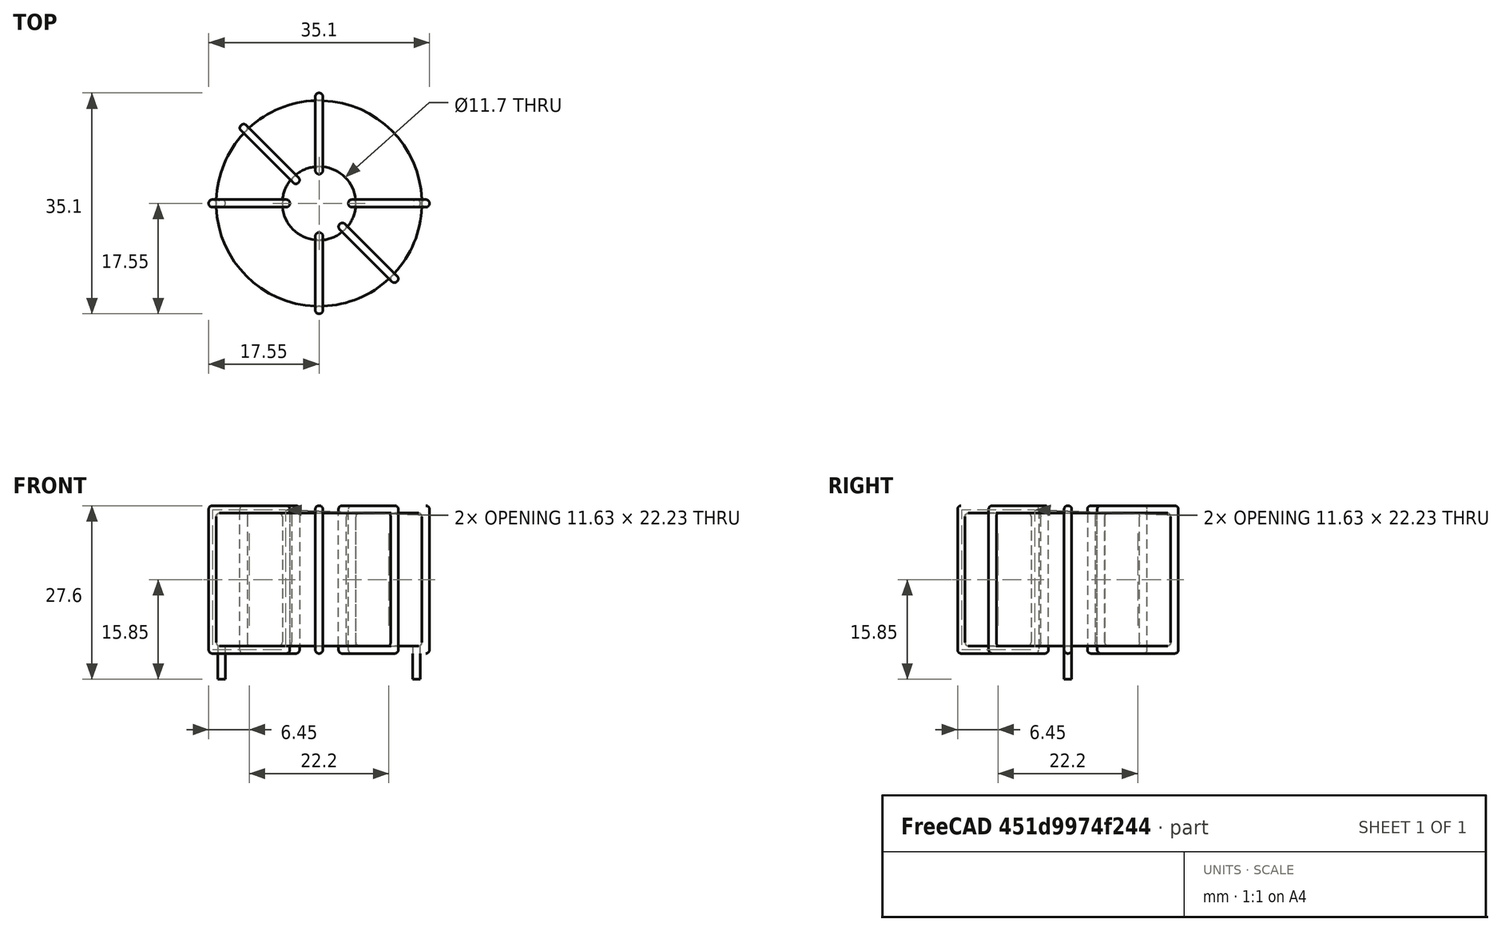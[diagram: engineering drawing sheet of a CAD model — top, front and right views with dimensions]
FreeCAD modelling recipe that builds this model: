
FCSTD DOCUMENT  (FreeCAD 0.16R6703 (Git))
Label: L_Toroid_Horizontal_D35.1mm_P31.00mm_Vishay_TJ6
License: All rights reserved
LicenseURL: http://en.wikipedia.org/wiki/All_rights_reserved
objects: Sketcher::SketchObject×6, PartDesign::Pad×6, PartDesign::Fillet×5, Spreadsheet::Sheet×1
note: 23 computed .brp shape members not serialized (recipe doc carries the construction recipe); baked Part::Feature solids carry a one-line shape summary decoded from their .brp

FEATURE [Spreadsheet::Sheet] Spreadsheet  label="dimensions"
  cells = A1=Wx; B1(Wx)=35.1; C1(WW)=11.7; D1=35.1; A2=Wy; B2(Wy)=35.1; D2=35.1; A3=RM; B3(RMx)=31; C3(RMy)=0; A4=d_wire; B4(d_wire)=1.2; A5=H; B5(H)=21.1; A6=offsetx; B6(offsetx)=2.050000000000001
FEATURE [Sketcher::SketchObject] Sketch
  Placement = pos=(0,0,1.7) rot=(0,0,1;0rad)
  expr: Placement.Base.z = 0.5 + Spreadsheet.d_wire
  expr: Constraints[0] = Spreadsheet.Wx / 2 - Spreadsheet.d_wire
  expr: Constraints[4] = Spreadsheet.WW / 2
  expr: Constraints[2] = Spreadsheet.RMy / 2
  expr: Constraints[1] = Spreadsheet.RMx / 2
  sketch-geometry (2):
    g0: Circle CenterX=15.5 CenterY=0 CenterZ=0 NormalX=0 NormalY=0 NormalZ=1 Radius=16.35
    g1: Circle CenterX=15.5 CenterY=0 CenterZ=0 NormalX=0 NormalY=0 NormalZ=1 Radius=5.85
  constraints (5):
    c: Radius(g0) = 16.35
    c: DistanceX(g-1,g0) = 15.5
    c: DistanceY(g-1,g0) = 0
    c: Coincident(g1,g0)
    c: Radius(g1) = 5.85
FEATURE [PartDesign::Pad] Pad
  Length = 21.1
  Length2 = 100
  Placement = pos=(0,0,1.7) rot=(0,0,1;0rad)
  Sketch = -> Sketch
  Type = 0
  expr: Length = Spreadsheet.H
FEATURE [Sketcher::SketchObject] Sketch001
  Placement = pos=(0,0,1.1) rot=(0,0,1;0rad)
  expr: Placement.Base.z = 0.5 + Spreadsheet.d_wire * 0.5
  expr: Constraints[4] = Spreadsheet.RMx
  expr: Constraints[2] = Spreadsheet.RMy
  expr: Constraints[1] = Spreadsheet.d_wire / 2
  sketch-geometry (2):
    g0: Circle CenterX=0 CenterY=0 CenterZ=0 NormalX=0 NormalY=0 NormalZ=1 Radius=0.6
    g1: Circle CenterX=31 CenterY=0 CenterZ=0 NormalX=0 NormalY=0 NormalZ=1 Radius=0.6
  constraints (5):
    c: Equal(g0,g1)
    c: Radius(g0) = 0.6
    c: DistanceY(g-1,g1) = 0
    c: Coincident(g0,g-1)
    c: DistanceX(g-1,g1) = 31
FEATURE [PartDesign::Pad] Pad001
  Length = 0.6
  Length2 = 4.7
  Placement = pos=(0,0,1.1) rot=(0,0,1;0rad)
  Reversed = true
  Sketch = -> Sketch001
  Type = 4
  expr: Length2 = 3.5 + Spreadsheet.d_wire
  expr: Length = Spreadsheet.d_wire / 2
FEATURE [PartDesign::Fillet] Fillet
  Base = -> Pad [Edge6,Edge3,Edge2]
  Placement = pos=(0,0,1.7) rot=(0,0,1;0rad)
  Radius = 0.5
FEATURE [Sketcher::SketchObject] Sketch003
  Placement = pos=(15.5,0,0) rot=(1,0,0;1.5708rad)
  expr: Placement.Base.x = Spreadsheet.RMx / 2
  expr: Constraints[49] = Spreadsheet.Wx - Spreadsheet.d_wire * 2
  expr: Constraints[44] = Spreadsheet.d_wire
  expr: Constraints[23] = Spreadsheet.H
  expr: Constraints[22] = Spreadsheet.Wx / 2 - Spreadsheet.d_wire
  expr: Placement.Base.y = Spreadsheet.RMy / 2
  expr: Constraints[21] = (Spreadsheet.Wx - Spreadsheet.WW) / 2 - Spreadsheet.d_wire
  expr: Constraints[19] = Spreadsheet.d_wire
  expr: Constraints[17] = Spreadsheet.d_wire
  expr: Constraints[18] = Spreadsheet.d_wire
  expr: Constraints[16] = Spreadsheet.d_wire
  sketch-geometry (16):
    g0: LineSegment StartX=-4.65 StartY=0.5 StartZ=0 EndX=-17.55 EndY=0.5 EndZ=0
    g1: LineSegment StartX=-17.55 StartY=0.5 StartZ=0 EndX=-17.55 EndY=24 EndZ=0
    g2: LineSegment StartX=-17.55 StartY=24 StartZ=0 EndX=-4.65 EndY=24 EndZ=0
    g3: LineSegment StartX=-4.65 StartY=24 StartZ=0 EndX=-4.65 EndY=0.5 EndZ=0
    g4: LineSegment StartX=-16.35 StartY=22.8 StartZ=0 EndX=-5.85 EndY=22.8 EndZ=0
    g5: LineSegment StartX=-5.85 StartY=22.8 StartZ=0 EndX=-5.85 EndY=1.7 EndZ=0
    g6: LineSegment StartX=-5.85 StartY=1.7 StartZ=0 EndX=-16.35 EndY=1.7 EndZ=0
    g7: LineSegment StartX=-16.35 StartY=1.7 StartZ=0 EndX=-16.35 EndY=22.8 EndZ=0
    g8: LineSegment StartX=4.65 StartY=24 StartZ=0 EndX=17.55 EndY=24 EndZ=0
    g9: LineSegment StartX=17.55 StartY=24 StartZ=0 EndX=17.55 EndY=0.5 EndZ=0
    g10: LineSegment StartX=17.55 StartY=0.5 StartZ=0 EndX=4.65 EndY=0.5 EndZ=0
    g11: LineSegment StartX=4.65 StartY=0.5 StartZ=0 EndX=4.65 EndY=24 EndZ=0
    g12: LineSegment StartX=5.85 StartY=22.8 StartZ=0 EndX=16.35 EndY=22.8 EndZ=0
    g13: LineSegment StartX=16.35 StartY=22.8 StartZ=0 EndX=16.35 EndY=1.7 EndZ=0
    g14: LineSegment StartX=16.35 StartY=1.7 StartZ=0 EndX=5.85 EndY=1.7 EndZ=0
    g15: LineSegment StartX=5.85 StartY=1.7 StartZ=0 EndX=5.85 EndY=22.8 EndZ=0
  constraints (50):
    c: Horizontal(g0)
    c: Coincident(g1,g0)
    c: Vertical(g1)
    c: Coincident(g2,g1)
    c: Horizontal(g2)
    c: Coincident(g3,g2)
    c: Coincident(g3,g0)
    c: Vertical(g3)
    c: Coincident(g4,g5)
    c: Coincident(g5,g6)
    c: Coincident(g6,g7)
    c: Coincident(g7,g4)
    c: Horizontal(g4)
    c: Horizontal(g6)
    c: Vertical(g5)
    c: Vertical(g7)
    c: DistanceX(g1,g4) = 1.2
    c: DistanceY(g4,g1) = 1.2
    c: DistanceX(g5,g0) = 1.2
    c: DistanceY(g0,g5) = 1.2
    c: DistanceY(g-1,g0) = 0.5
    c: DistanceX(g6,g6) = 10.5
    c: DistanceX(g6,g-1) = 16.35
    c: DistanceY(g7,g7) = 21.1
    c: Coincident(g8,g9)
    c: Coincident(g9,g10)
    c: Coincident(g10,g11)
    c: Coincident(g11,g8)
    c: Horizontal(g8)
    c: Horizontal(g10)
    c: Vertical(g9)
    c: Vertical(g11)
    c: Coincident(g12,g13)
    c: Coincident(g13,g14)
    c: Coincident(g14,g15)
    c: Coincident(g15,g12)
    c: Horizontal(g12)
    c: Horizontal(g14)
    c: Vertical(g13)
    c: Vertical(g15)
    c: DistanceY(g8,g2) = 0
    c: DistanceY(g10,g0) = 0
    c: DistanceY(g14,g5) = 0
    c: DistanceY(g12,g4) = 0
    c: DistanceX(g8,g12) = 1.2
    c: Equal(g8,g2)
    c: Equal(g12,g4)
    c: Equal(g9,g1)
    c: Equal(g13,g7)
    c: DistanceX(g4,g12) = 32.7
FEATURE [PartDesign::Pad] Pad002
  Length = 1.2
  Length2 = 100
  Midplane = true
  Placement = pos=(15.5,0,0) rot=(1,0,0;1.5708rad)
  Sketch = -> Sketch003
  Type = 0
  expr: Length = Spreadsheet.d_wire
FEATURE [PartDesign::Fillet] Fillet001
  Base = -> Pad002 [Edge38,Edge41,Edge42,Edge43,Edge29,Edge32,Edge33,Edge34,Edge25,Edge35,Edge36,Edge13,Edge14,Edge15,Edge16,Edge17,Edge18,Edge19,Edge1,Edge2,Edge3,Edge4,Edge5,Edge6,Edge7,Edge37,Edge39,Edge40,Edge20,Edge23,Edge24,Edge21,Edge22,Edge8,Edge9,Edge10,Edge11,Edge12,Edge26,Edge27,+8 more]
  Placement = pos=(15.5,0,0) rot=(1,0,0;1.5708rad)
  Radius = 0.564
  expr: Radius = Spreadsheet.d_wire * 0.47
FEATURE [Sketcher::SketchObject] Sketch004
  Placement = pos=(15.5,0,0) rot=(0.862856,0.357407,0.357407;1.71777rad)
  expr: Placement.Base.x = Spreadsheet.RMx / 2
  expr: Constraints[49] = Spreadsheet.Wx - 2 * Spreadsheet.d_wire
  expr: Constraints[44] = Spreadsheet.d_wire
  expr: Constraints[23] = Spreadsheet.H
  expr: Constraints[22] = Spreadsheet.Wx / 2 - Spreadsheet.d_wire
  expr: Placement.Base.y = Spreadsheet.RMy / 2
  expr: Constraints[21] = (Spreadsheet.Wx - Spreadsheet.WW) / 2 - Spreadsheet.d_wire
  expr: Constraints[19] = Spreadsheet.d_wire
  expr: Constraints[17] = Spreadsheet.d_wire
  expr: Constraints[18] = Spreadsheet.d_wire
  expr: Constraints[16] = Spreadsheet.d_wire
  sketch-geometry (16):
    g0: LineSegment StartX=-4.65 StartY=0.5 StartZ=0 EndX=-17.55 EndY=0.5 EndZ=0
    g1: LineSegment StartX=-17.55 StartY=0.5 StartZ=0 EndX=-17.55 EndY=24 EndZ=0
    g2: LineSegment StartX=-17.55 StartY=24 StartZ=0 EndX=-4.65 EndY=24 EndZ=0
    g3: LineSegment StartX=-4.65 StartY=24 StartZ=0 EndX=-4.65 EndY=0.5 EndZ=0
    g4: LineSegment StartX=-16.35 StartY=22.8 StartZ=0 EndX=-5.85 EndY=22.8 EndZ=0
    g5: LineSegment StartX=-5.85 StartY=22.8 StartZ=0 EndX=-5.85 EndY=1.7 EndZ=0
    g6: LineSegment StartX=-5.85 StartY=1.7 StartZ=0 EndX=-16.35 EndY=1.7 EndZ=0
    g7: LineSegment StartX=-16.35 StartY=1.7 StartZ=0 EndX=-16.35 EndY=22.8 EndZ=0
    g8: LineSegment StartX=4.65 StartY=24 StartZ=0 EndX=17.55 EndY=24 EndZ=0
    g9: LineSegment StartX=17.55 StartY=24 StartZ=0 EndX=17.55 EndY=0.5 EndZ=0
    g10: LineSegment StartX=17.55 StartY=0.5 StartZ=0 EndX=4.65 EndY=0.5 EndZ=0
    g11: LineSegment StartX=4.65 StartY=0.5 StartZ=0 EndX=4.65 EndY=24 EndZ=0
    g12: LineSegment StartX=5.85 StartY=22.8 StartZ=0 EndX=16.35 EndY=22.8 EndZ=0
    g13: LineSegment StartX=16.35 StartY=22.8 StartZ=0 EndX=16.35 EndY=1.7 EndZ=0
    g14: LineSegment StartX=16.35 StartY=1.7 StartZ=0 EndX=5.85 EndY=1.7 EndZ=0
    g15: LineSegment StartX=5.85 StartY=1.7 StartZ=0 EndX=5.85 EndY=22.8 EndZ=0
  constraints (50):
    c: Horizontal(g0)
    c: Coincident(g1,g0)
    c: Vertical(g1)
    c: Coincident(g2,g1)
    c: Horizontal(g2)
    c: Coincident(g3,g2)
    c: Coincident(g3,g0)
    c: Vertical(g3)
    c: Coincident(g4,g5)
    c: Coincident(g5,g6)
    c: Coincident(g6,g7)
    c: Coincident(g7,g4)
    c: Horizontal(g4)
    c: Horizontal(g6)
    c: Vertical(g5)
    c: Vertical(g7)
    c: DistanceX(g1,g4) = 1.2
    c: DistanceY(g4,g1) = 1.2
    c: DistanceX(g5,g0) = 1.2
    c: DistanceY(g0,g5) = 1.2
    c: DistanceY(g-1,g0) = 0.5
    c: DistanceX(g6,g6) = 10.5
    c: DistanceX(g6,g-1) = 16.35
    c: DistanceY(g7,g7) = 21.1
    c: Coincident(g8,g9)
    c: Coincident(g9,g10)
    c: Coincident(g10,g11)
    c: Coincident(g11,g8)
    c: Horizontal(g8)
    c: Horizontal(g10)
    c: Vertical(g9)
    c: Vertical(g11)
    c: Coincident(g12,g13)
    c: Coincident(g13,g14)
    c: Coincident(g14,g15)
    c: Coincident(g15,g12)
    c: Horizontal(g12)
    c: Horizontal(g14)
    c: Vertical(g13)
    c: Vertical(g15)
    c: DistanceY(g8,g2) = 0
    c: DistanceY(g10,g0) = 0
    c: DistanceY(g14,g5) = 0
    c: DistanceY(g12,g4) = 0
    c: DistanceX(g8,g12) = 1.2
    c: Equal(g8,g2)
    c: Equal(g12,g4)
    c: Equal(g9,g1)
    c: Equal(g13,g7)
    c: DistanceX(g4,g12) = 32.7
FEATURE [PartDesign::Pad] Pad003
  Length = 1.2
  Length2 = 100
  Midplane = true
  Placement = pos=(15.5,0,0) rot=(0.862856,0.357407,0.357407;1.71777rad)
  Sketch = -> Sketch004
  Type = 0
  expr: Length = Spreadsheet.d_wire
FEATURE [PartDesign::Fillet] Fillet002
  Base = -> Pad003 [Edge38,Edge41,Edge42,Edge43,Edge29,Edge32,Edge33,Edge34,Edge25,Edge35,Edge36,Edge13,Edge14,Edge15,Edge16,Edge17,Edge18,Edge19,Edge1,Edge2,Edge3,Edge4,Edge5,Edge6,Edge7,Edge37,Edge39,Edge40,Edge20,Edge23,Edge24,Edge21,Edge22,Edge8,Edge9,Edge10,Edge11,Edge12,Edge26,Edge27,+8 more]
  Placement = pos=(15.5,0,0) rot=(0.862856,0.357407,0.357407;1.71777rad)
  Radius = 0.564
  expr: Radius = Spreadsheet.d_wire * 0.47
FEATURE [Sketcher::SketchObject] Sketch005
  Placement = pos=(15.5,0,0) rot=(0.862856,-0.357407,-0.357407;1.71777rad)
  expr: Placement.Base.x = Spreadsheet.RMx / 2
  expr: Constraints[49] = Spreadsheet.Wx - 2 * Spreadsheet.d_wire
  expr: Constraints[44] = Spreadsheet.d_wire
  expr: Constraints[23] = Spreadsheet.H
  expr: Constraints[22] = Spreadsheet.Wx / 2 - Spreadsheet.d_wire
  expr: Placement.Base.y = Spreadsheet.RMy / 2
  expr: Constraints[21] = (Spreadsheet.Wx - Spreadsheet.WW) / 2 - Spreadsheet.d_wire
  expr: Constraints[19] = Spreadsheet.d_wire
  expr: Constraints[17] = Spreadsheet.d_wire
  expr: Constraints[18] = Spreadsheet.d_wire
  expr: Constraints[16] = Spreadsheet.d_wire
  sketch-geometry (16):
    g0: LineSegment StartX=-4.65 StartY=0.5 StartZ=0 EndX=-17.55 EndY=0.5 EndZ=0
    g1: LineSegment StartX=-17.55 StartY=0.5 StartZ=0 EndX=-17.55 EndY=24 EndZ=0
    g2: LineSegment StartX=-17.55 StartY=24 StartZ=0 EndX=-4.65 EndY=24 EndZ=0
    g3: LineSegment StartX=-4.65 StartY=24 StartZ=0 EndX=-4.65 EndY=0.5 EndZ=0
    g4: LineSegment StartX=-16.35 StartY=22.8 StartZ=0 EndX=-5.85 EndY=22.8 EndZ=0
    g5: LineSegment StartX=-5.85 StartY=22.8 StartZ=0 EndX=-5.85 EndY=1.7 EndZ=0
    g6: LineSegment StartX=-5.85 StartY=1.7 StartZ=0 EndX=-16.35 EndY=1.7 EndZ=0
    g7: LineSegment StartX=-16.35 StartY=1.7 StartZ=0 EndX=-16.35 EndY=22.8 EndZ=0
    g8: LineSegment StartX=4.65 StartY=24 StartZ=0 EndX=17.55 EndY=24 EndZ=0
    g9: LineSegment StartX=17.55 StartY=24 StartZ=0 EndX=17.55 EndY=0.5 EndZ=0
    g10: LineSegment StartX=17.55 StartY=0.5 StartZ=0 EndX=4.65 EndY=0.5 EndZ=0
    g11: LineSegment StartX=4.65 StartY=0.5 StartZ=0 EndX=4.65 EndY=24 EndZ=0
    g12: LineSegment StartX=5.85 StartY=22.8 StartZ=0 EndX=16.35 EndY=22.8 EndZ=0
    g13: LineSegment StartX=16.35 StartY=22.8 StartZ=0 EndX=16.35 EndY=1.7 EndZ=0
    g14: LineSegment StartX=16.35 StartY=1.7 StartZ=0 EndX=5.85 EndY=1.7 EndZ=0
    g15: LineSegment StartX=5.85 StartY=1.7 StartZ=0 EndX=5.85 EndY=22.8 EndZ=0
  constraints (50):
    c: Horizontal(g0)
    c: Coincident(g1,g0)
    c: Vertical(g1)
    c: Coincident(g2,g1)
    c: Horizontal(g2)
    c: Coincident(g3,g2)
    c: Coincident(g3,g0)
    c: Vertical(g3)
    c: Coincident(g4,g5)
    c: Coincident(g5,g6)
    c: Coincident(g6,g7)
    c: Coincident(g7,g4)
    c: Horizontal(g4)
    c: Horizontal(g6)
    c: Vertical(g5)
    c: Vertical(g7)
    c: DistanceX(g1,g4) = 1.2
    c: DistanceY(g4,g1) = 1.2
    c: DistanceX(g5,g0) = 1.2
    c: DistanceY(g0,g5) = 1.2
    c: DistanceY(g-1,g0) = 0.5
    c: DistanceX(g6,g6) = 10.5
    c: DistanceX(g6,g-1) = 16.35
    c: DistanceY(g7,g7) = 21.1
    c: Coincident(g8,g9)
    c: Coincident(g9,g10)
    c: Coincident(g10,g11)
    c: Coincident(g11,g8)
    c: Horizontal(g8)
    c: Horizontal(g10)
    c: Vertical(g9)
    c: Vertical(g11)
    c: Coincident(g12,g13)
    c: Coincident(g13,g14)
    c: Coincident(g14,g15)
    c: Coincident(g15,g12)
    c: Horizontal(g12)
    c: Horizontal(g14)
    c: Vertical(g13)
    c: Vertical(g15)
    c: DistanceY(g8,g2) = 0
    c: DistanceY(g10,g0) = 0
    c: DistanceY(g14,g5) = 0
    c: DistanceY(g12,g4) = 0
    c: DistanceX(g8,g12) = 1.2
    c: Equal(g8,g2)
    c: Equal(g12,g4)
    c: Equal(g9,g1)
    c: Equal(g13,g7)
    c: DistanceX(g4,g12) = 32.7
FEATURE [PartDesign::Pad] Pad004
  Length = 1.2
  Length2 = 100
  Midplane = true
  Placement = pos=(15.5,0,0) rot=(0.862856,-0.357407,-0.357407;1.71777rad)
  Sketch = -> Sketch005
  Type = 0
  expr: Length = Spreadsheet.d_wire
FEATURE [PartDesign::Fillet] Fillet003
  Base = -> Pad004 [Edge38,Edge41,Edge42,Edge43,Edge29,Edge32,Edge33,Edge34,Edge25,Edge35,Edge36,Edge13,Edge14,Edge15,Edge16,Edge17,Edge18,Edge19,Edge1,Edge2,Edge3,Edge4,Edge5,Edge6,Edge7,Edge37,Edge39,Edge40,Edge20,Edge23,Edge24,Edge21,Edge22,Edge8,Edge9,Edge10,Edge11,Edge12,Edge26,Edge27,+8 more]
  Placement = pos=(15.5,0,0) rot=(0.862856,-0.357407,-0.357407;1.71777rad)
  Radius = 0.564
  expr: Radius = Spreadsheet.d_wire * 0.47
FEATURE [Sketcher::SketchObject] Sketch006
  Placement = pos=(15.5,0,0) rot=(0.57735,0.57735,0.57735;2.0944rad)
  expr: Placement.Base.x = Spreadsheet.RMx / 2
  expr: Constraints[49] = Spreadsheet.Wx - Spreadsheet.d_wire * 2
  expr: Constraints[44] = Spreadsheet.d_wire
  expr: Constraints[23] = Spreadsheet.H
  expr: Constraints[22] = Spreadsheet.Wx / 2 - Spreadsheet.d_wire
  expr: Placement.Base.y = Spreadsheet.RMy / 2
  expr: Constraints[21] = (Spreadsheet.Wx - Spreadsheet.WW) / 2 - Spreadsheet.d_wire
  expr: Constraints[19] = Spreadsheet.d_wire
  expr: Constraints[17] = Spreadsheet.d_wire
  expr: Constraints[18] = Spreadsheet.d_wire
  expr: Constraints[16] = Spreadsheet.d_wire
  sketch-geometry (16):
    g0: LineSegment StartX=-4.65 StartY=0.5 StartZ=0 EndX=-17.55 EndY=0.5 EndZ=0
    g1: LineSegment StartX=-17.55 StartY=0.5 StartZ=0 EndX=-17.55 EndY=24 EndZ=0
    g2: LineSegment StartX=-17.55 StartY=24 StartZ=0 EndX=-4.65 EndY=24 EndZ=0
    g3: LineSegment StartX=-4.65 StartY=24 StartZ=0 EndX=-4.65 EndY=0.5 EndZ=0
    g4: LineSegment StartX=-16.35 StartY=22.8 StartZ=0 EndX=-5.85 EndY=22.8 EndZ=0
    g5: LineSegment StartX=-5.85 StartY=22.8 StartZ=0 EndX=-5.85 EndY=1.7 EndZ=0
    g6: LineSegment StartX=-5.85 StartY=1.7 StartZ=0 EndX=-16.35 EndY=1.7 EndZ=0
    g7: LineSegment StartX=-16.35 StartY=1.7 StartZ=0 EndX=-16.35 EndY=22.8 EndZ=0
    g8: LineSegment StartX=4.65 StartY=24 StartZ=0 EndX=17.55 EndY=24 EndZ=0
    g9: LineSegment StartX=17.55 StartY=24 StartZ=0 EndX=17.55 EndY=0.5 EndZ=0
    g10: LineSegment StartX=17.55 StartY=0.5 StartZ=0 EndX=4.65 EndY=0.5 EndZ=0
    g11: LineSegment StartX=4.65 StartY=0.5 StartZ=0 EndX=4.65 EndY=24 EndZ=0
    g12: LineSegment StartX=5.85 StartY=22.8 StartZ=0 EndX=16.35 EndY=22.8 EndZ=0
    g13: LineSegment StartX=16.35 StartY=22.8 StartZ=0 EndX=16.35 EndY=1.7 EndZ=0
    g14: LineSegment StartX=16.35 StartY=1.7 StartZ=0 EndX=5.85 EndY=1.7 EndZ=0
    g15: LineSegment StartX=5.85 StartY=1.7 StartZ=0 EndX=5.85 EndY=22.8 EndZ=0
  constraints (50):
    c: Horizontal(g0)
    c: Coincident(g1,g0)
    c: Vertical(g1)
    c: Coincident(g2,g1)
    c: Horizontal(g2)
    c: Coincident(g3,g2)
    c: Coincident(g3,g0)
    c: Vertical(g3)
    c: Coincident(g4,g5)
    c: Coincident(g5,g6)
    c: Coincident(g6,g7)
    c: Coincident(g7,g4)
    c: Horizontal(g4)
    c: Horizontal(g6)
    c: Vertical(g5)
    c: Vertical(g7)
    c: DistanceX(g1,g4) = 1.2
    c: DistanceY(g4,g1) = 1.2
    c: DistanceX(g5,g0) = 1.2
    c: DistanceY(g0,g5) = 1.2
    c: DistanceY(g-1,g0) = 0.5
    c: DistanceX(g6,g6) = 10.5
    c: DistanceX(g6,g-1) = 16.35
    c: DistanceY(g7,g7) = 21.1
    c: Coincident(g8,g9)
    c: Coincident(g9,g10)
    c: Coincident(g10,g11)
    c: Coincident(g11,g8)
    c: Horizontal(g8)
    c: Horizontal(g10)
    c: Vertical(g9)
    c: Vertical(g11)
    c: Coincident(g12,g13)
    c: Coincident(g13,g14)
    c: Coincident(g14,g15)
    c: Coincident(g15,g12)
    c: Horizontal(g12)
    c: Horizontal(g14)
    c: Vertical(g13)
    c: Vertical(g15)
    c: DistanceY(g8,g2) = 0
    c: DistanceY(g10,g0) = 0
    c: DistanceY(g14,g5) = 0
    c: DistanceY(g12,g4) = 0
    c: DistanceX(g8,g12) = 1.2
    c: Equal(g8,g2)
    c: Equal(g12,g4)
    c: Equal(g9,g1)
    c: Equal(g13,g7)
    c: DistanceX(g4,g12) = 32.7
FEATURE [PartDesign::Pad] Pad005
  Length = 1.2
  Length2 = 100
  Midplane = true
  Placement = pos=(15.5,0,0) rot=(0.57735,0.57735,0.57735;2.0944rad)
  Sketch = -> Sketch006
  Type = 0
  expr: Length = Spreadsheet.d_wire
FEATURE [PartDesign::Fillet] Fillet004
  Base = -> Pad005 [Edge38,Edge41,Edge42,Edge43,Edge29,Edge32,Edge33,Edge34,Edge25,Edge35,Edge36,Edge13,Edge14,Edge15,Edge16,Edge17,Edge18,Edge19,Edge1,Edge2,Edge3,Edge4,Edge5,Edge6,Edge7,Edge37,Edge39,Edge40,Edge20,Edge23,Edge24,Edge21,Edge22,Edge8,Edge9,Edge10,Edge11,Edge12,Edge26,Edge27,+8 more]
  Placement = pos=(15.5,0,0) rot=(0.57735,0.57735,0.57735;2.0944rad)
  Radius = 0.564
  expr: Radius = Spreadsheet.d_wire * 0.47
